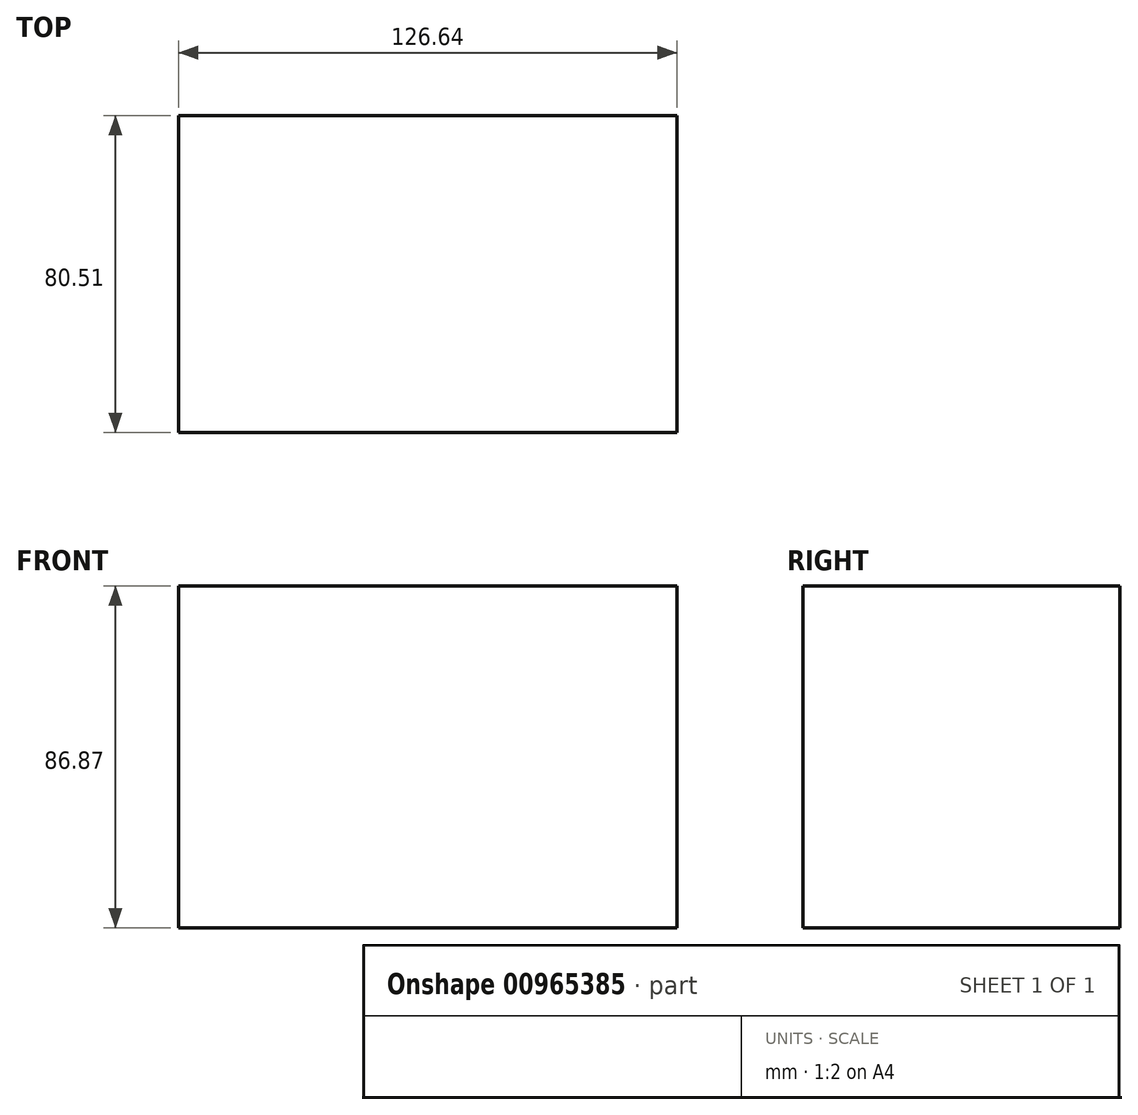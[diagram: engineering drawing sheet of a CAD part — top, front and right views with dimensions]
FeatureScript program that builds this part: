
annotation { "Feature Type Name" : "Feature", "Feature Type Description" : "" }
export const myFeature = defineFeature(function(context is Context, id is Id, definition is map)
    precondition{}
    {
        {
            var Q0;
            Q0=qCreatedBy(makeId("Top.planeOp"),FACE);
            var sketch = newSketch(context, id + "F0", { "sketchPlane" : qUnion([Q0])});
            skLineSegment(sketch, "E0.bottom", {"start": v(-68.56, 43.2) * mm, "end": v(58.08, 43.2) * mm});
            skLineSegment(sketch, "E0.top", {"start": v(-68.56, -37.3) * mm, "end": v(58.08, -37.3) * mm});
            skLineSegment(sketch, "E0.left", {"start": v(-68.56, 43.2) * mm, "end": v(-68.56, -37.3) * mm});
            skLineSegment(sketch, "E0.right", {"start": v(58.08, 43.2) * mm, "end": v(58.08, -37.3) * mm});
            skSolve(sketch);
        }
        {
            var Q0;
            Q0=makeQuery(id+"F0.imprint","IMPRINT",FACE,{"disambiguationData":[TD([[makeQuery(id+"F0.imprint","IMPRINT",EDGE,{"derivedFrom":sQuery(id+"F0.wireOp",EDGE,"E0.bottom")}),-1.0]])]});
            extrude(context, id + "F1", {"entities" : qUnion([Q0]), "depth" : 86.87 * mm, "offsetDistance" : 25.4 * mm});
        }
    });
